# Revit family: P703
name_source: partatom
category: Specialty Equipment
revit_build: Autodesk Revit Architecture 2012 (Build: 20110309_2315(x64)
units: mm (PartAtom-declared; Revit-internal decimal feet)

## types (1)
- P703
    Additional Features = See brochure
    Back Circuit Panel Height = 20.05 "
    Back Circuit Panel Height from Bottom = 3.17 "
    Back Circuit Panel Width = 35.43 "
    Connectivity- Digital Tuner = P703-AVT
    Connectivity- Input Terminals. Analog = VGA 15-pin D-sub
    Connectivity- Input Terminals. Audio = Audio Mini-Jack, DisplayPort Audio, HDMI Audio
    Connectivity- Input Terminals. Digital = Display Port, HDMI, DVI-D
    Connectivity- Input Terminals. External Control = RS-232C, LAN, DDC/CI
    Connectivity- Output Terminals. Audio = Audio Mini-Jack, External Speaker Jack (2)
    Connectivity- Output Terminals. Digital = DisplayPort
    Connectivity- Output Terminals. External Control = RS-232C
    Connectivity- PC/Mac Signal Compatibility = Yes
    Environmental Conditions- Operating Altitude = 9843ft / 3000m
    Environmental Conditions- Operating Humidity = 20-80%
    Environmental Conditions- Operating Temperature = 32-122 degF / 0-50 degC
    Height from Floor = 26 "
    LCD- Active Screen Area (W x H) = TBD
    LCD- Aspect Ratio = 16 : 9
    LCD- Backlight Type = LED Edge-lit
    LCD- Brightness (Typical/Max) = 550/700 cd/m2
    LCD- Contrast Ratio (Typical) = 4000 : 1
    LCD- Displayable Colors = More than 16.7 Million
    LCD- Native Resolution = 1920 x 1080
    LCD- Orientation = Landscape / Portrait
    LCD- Panel Technology = SPVA (P-DID)
    LCD- Response Time (G-to-G) = 8ms
    LCD- Viewable Image Size = 70"
    LCD- Viewing Angle = 178deg Vert., 178deg Hor. (89U/89D/89L/89R) at CR>10
    Limited Warranty = 3 years parts and labor, including backlight
    Manufacturer = NEC Display
    Optional Accessories = See brochure
    Panel Height = 36.2 "
    Panel Thickness = 1.11 "
    Panel Thickness Overall = 2.73 "
    Panel Width = 0.64 "
    Panel Width Overall = 62.48 "
    Physical Specs- Bezel Width (L/R, T/B) = 0.6In/0.6in, 0.6in/0.6in; 15.5mm/15.5mm, 15.5mm/15.5mm
    Physical Specs- Net Dimensions (w/o stand- WxHxD) = 62.5 x 36.2 x 3.4in / 1587 x 919.6 x 86.9mm
    Physical Specs- Net Weight (w/o stand) = 105.1 lbs / 47.8 kgs
    Physical Specs- VESA Hole Configuration = 400 x 400mm
    Power Consumption- ECO Mode Standby = <0.5W
    Power Consumption- On (Typical) = TBD
    Ships with = See brochure
    URL = necdisplay.com
    c1 = 2.26 "
    c2 = 0.12 "

## geometry (parser evidence)
native form markers: Blend x9, Sweep x44
no freeform markers — native parametric forms only
